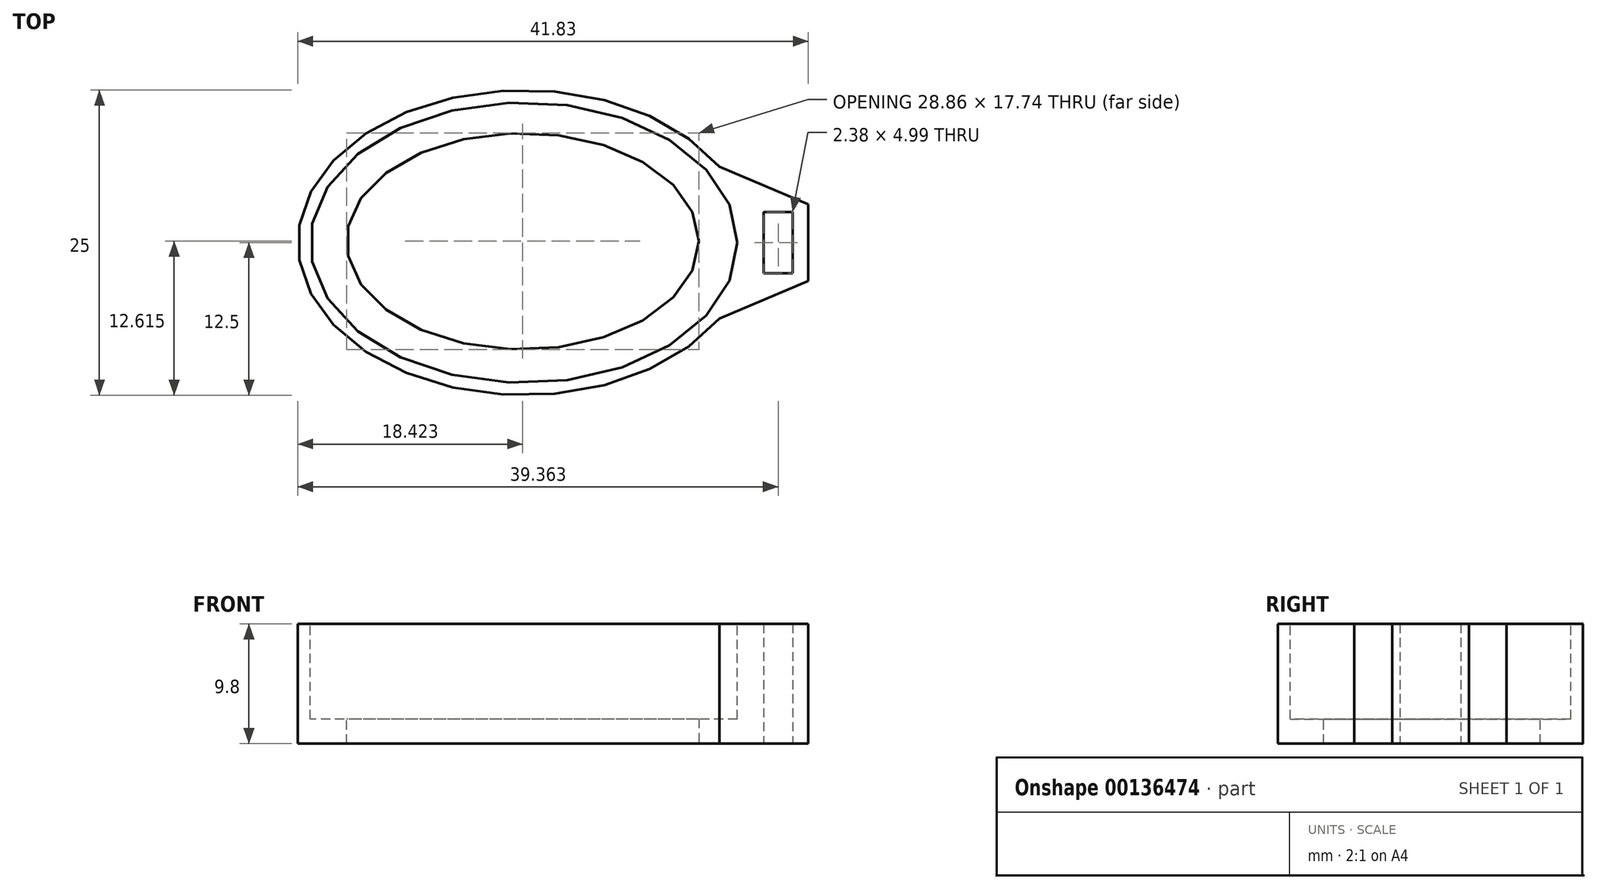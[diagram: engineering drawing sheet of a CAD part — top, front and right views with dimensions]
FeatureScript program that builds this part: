
annotation { "Feature Type Name" : "Feature", "Feature Type Description" : "" }
export const myFeature = defineFeature(function(context is Context, id is Id, definition is map)
    precondition{}
    {
        {
            var Q0;
            Q0=qCreatedBy(makeId("Top.planeOp"),FACE);
            var sketch = newSketch(context, id + "F0", { "sketchPlane" : qUnion([Q0])});
            skEllipse(sketch, "E0", {"center": v(0, 0) * mm, "majorRadius": 17.5 * mm, "minorRadius": 11.5 * mm, "majorAxis": v(1, 0)});
            skEllipse(sketch, "E1", {"center": v(0, 0) * mm, "majorRadius": 18.5 * mm, "minorRadius": 12.5 * mm, "majorAxis": v(1, 0)});
            skEllipse(sketch, "E2", {"center": v(-0.09, 0.12) * mm, "majorRadius": 14.43 * mm, "minorRadius": 8.87 * mm, "majorAxis": v(1, 0)});
            skPoint(sketch, "E3.middle", {"position": v(18.5, 0) * mm});
            skPoint(sketch, "E4.middle", {"position": v(29.4, 0) * mm});
            skLineSegment(sketch, "E5", {"start": v(23.32, 0) * mm, "end": v(23.32, -3.15) * mm});
            skLineSegment(sketch, "E6", {"start": v(23.32, -3.15) * mm, "end": v(16.03, -6.23) * mm});
            skLineSegment(sketch, "E7.MirrorCS", {"start": v(23.32, 3.15) * mm, "end": v(16.03, 6.23) * mm});
            skLineSegment(sketch, "E8.MirrorCS", {"start": v(23.32, 0) * mm, "end": v(23.32, 3.15) * mm});
            skLineSegment(sketch, "E9.bottom", {"start": v(22.04, -2.5) * mm, "end": v(19.67, -2.5) * mm});
            skLineSegment(sketch, "E9.top", {"start": v(22.04, 2.5) * mm, "end": v(19.67, 2.5) * mm});
            skLineSegment(sketch, "E9.left", {"start": v(22.04, -2.5) * mm, "end": v(22.04, 2.5) * mm});
            skLineSegment(sketch, "E9.right", {"start": v(19.67, -2.5) * mm, "end": v(19.67, 2.5) * mm});
            skPoint(sketch, "E9.middle", {"position": v(20.85, 0) * mm});
            skSolve(sketch);
        }
        {
            var Q0;
            Q0=makeQuery(id+"F0.imprint","IMPRINT",FACE,{"disambiguationData":[TD([[makeQuery(id+"F0.imprint","IMPRINT",EDGE,{"derivedFrom":sQuery(id+"F0.wireOp",EDGE,"E5")}),-1.0]])]});
            var Q1;
            Q1=makeQuery(id+"F0.imprint","IMPRINT",FACE,{"disambiguationData":[TD([[makeQuery(id+"F0.imprint","IMPRINT",EDGE,{"derivedFrom":sQuery(id+"F0.wireOp",EDGE,"E0")}),-1.0]])]});
            var Q2;
            Q2=makeQuery(id+"F0.imprint","IMPRINT",FACE,{"disambiguationData":[TD([[makeQuery(id+"F0.imprint","IMPRINT",EDGE,{"derivedFrom":sQuery(id+"F0.wireOp",EDGE,"E0")}),1.0]])]});
            extrude(context, id + "F1", {"entities" : qUnion([Q0, Q1, Q2]), "depth" : 4 * mm});
        }
        {
            var Q0;
            Q0=makeQuery(id+"F1.opExtrude","CAP_FACE",FACE,{"disambiguationData":[OSD([sQuery(id+"F0.wireOp",EDGE,"E1"),sQuery(id+"F0.wireOp",EDGE,"E2"),sQuery(id+"F0.wireOp",EDGE,"E5"),sQuery(id+"F0.wireOp",EDGE,"E6"),sQuery(id+"F0.wireOp",EDGE,"E7.MirrorCS"),sQuery(id+"F0.wireOp",EDGE,"E8.MirrorCS"),sQuery(id+"F0.wireOp",EDGE,"E9.bottom"),sQuery(id+"F0.wireOp",EDGE,"E9.top"),sQuery(id+"F0.wireOp",EDGE,"E9.left"),sQuery(id+"F0.wireOp",EDGE,"E9.right")])],"isStart":false});
            var sketch = newSketch(context, id + "F2", { "sketchPlane" : qUnion([Q0])});
            skEllipse(sketch, "E10", {"center": v(0, 0) * mm, "majorRadius": 17.5 * mm, "minorRadius": 11.5 * mm, "majorAxis": v(1, 0)});
            skSolve(sketch);
        }
        {
            var Q0;
            Q0 = qSketchRegion(id + "F2", true);
            extrude(context, id + "F3", {"entities" : qUnion([Q0]), "operationType" : NewBodyOperationType.REMOVE, "oppositeDirection" : true, "depth" : 2 * mm});
        }
        {
            var Q0;
            Q0 = qSketchRegion(id + "F0", true);
            extrude(context, id + "F4", {"entities" : qUnion([Q0]), "operationType" : NewBodyOperationType.ADD, "depth" : 9.8 * mm});
        }
    });
